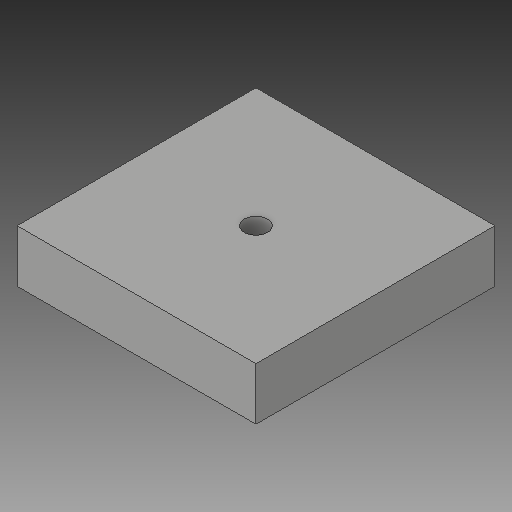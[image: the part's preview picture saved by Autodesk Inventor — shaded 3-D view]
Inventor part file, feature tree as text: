
AUTODESK INVENTOR PART (.ipt)
format: ipt  version: 2019 (Build 230136000, 136)  size: 98,816 bytes
history: native  units: mm
features: extrude x1, sketch x1
ambient origin geometry x8: Origin, YZ Plane, XZ Plane, XY Plane, X Axis, Y Axis, Z Axis, Center Point
bodies: Solid1 (feature_tree)
feature tree (2):
  extrude  "Extrusion1"  Depth=9.0mm
  sketch  "Sketch1"  dims[d0=41.0mm d1=4.0mm d2=9.0mm d3=0.0mm]
